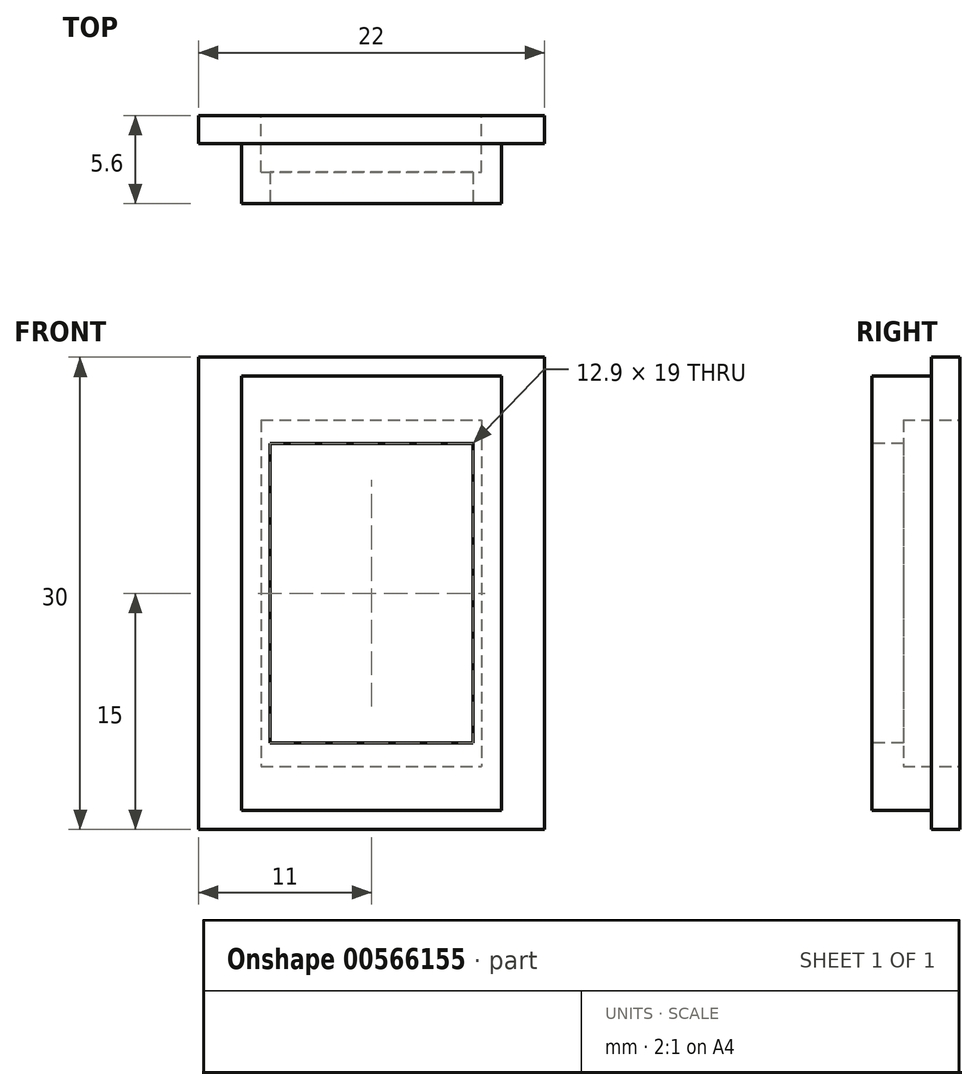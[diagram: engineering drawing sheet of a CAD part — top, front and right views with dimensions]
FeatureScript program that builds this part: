
annotation { "Feature Type Name" : "Feature", "Feature Type Description" : "" }
export const myFeature = defineFeature(function(context is Context, id is Id, definition is map)
    precondition{}
    {
        {
            var Q0;
            Q0=qCreatedBy(makeId("Front.planeOp"),FACE);
            var sketch = newSketch(context, id + "F0", { "sketchPlane" : qUnion([Q0])});
            skLineSegment(sketch, "E0.bottom", {"start": v(11, 15) * mm, "end": v(-11, 15) * mm});
            skLineSegment(sketch, "E0.top", {"start": v(11, -15) * mm, "end": v(-11, -15) * mm});
            skLineSegment(sketch, "E0.left", {"start": v(11, 15) * mm, "end": v(11, -15) * mm});
            skLineSegment(sketch, "E0.right", {"start": v(-11, 15) * mm, "end": v(-11, -15) * mm});
            skPoint(sketch, "E0.middle", {"position": v(0, 0) * mm});
            skSolve(sketch);
        }
        {
            var Q0;
            Q0 = qSketchRegion(id + "F0", true);
            extrude(context, id + "F1", {"entities" : qUnion([Q0]), "depth" : 1.8 * mm, "offsetDistance" : 25 * mm});
        }
        {
            var Q0;
            Q0=makeQuery(id+"F1.opExtrude","CAP_FACE",FACE,{"disambiguationData":[OSD([sQuery(id+"F0.wireOp",EDGE,"E0.bottom"),sQuery(id+"F0.wireOp",EDGE,"E0.top"),sQuery(id+"F0.wireOp",EDGE,"E0.left"),sQuery(id+"F0.wireOp",EDGE,"E0.right")])],"isStart":false});
            var sketch = newSketch(context, id + "F2", { "sketchPlane" : qUnion([Q0])});
            skLineSegment(sketch, "E1.bottom", {"start": v(8.25, 13.8) * mm, "end": v(-8.25, 13.8) * mm});
            skLineSegment(sketch, "E1.top", {"start": v(8.25, -13.8) * mm, "end": v(-8.25, -13.8) * mm});
            skLineSegment(sketch, "E1.left", {"start": v(8.25, 13.8) * mm, "end": v(8.25, -13.8) * mm});
            skLineSegment(sketch, "E1.right", {"start": v(-8.25, 13.8) * mm, "end": v(-8.25, -13.8) * mm});
            skPoint(sketch, "E1.middle", {"position": v(0, 0) * mm});
            skSolve(sketch);
        }
        {
            var Q0;
            Q0 = qSketchRegion(id + "F2", true);
            extrude(context, id + "F3", {"entities" : qUnion([Q0]), "operationType" : NewBodyOperationType.ADD, "depth" : 3.8 * mm, "offsetDistance" : 25 * mm});
        }
        {
            var Q0;
            Q0=makeQuery(id+"F3.opExtrude","CAP_FACE",FACE,{"disambiguationData":[OSD([sQuery(id+"F2.wireOp",EDGE,"E1.bottom"),sQuery(id+"F2.wireOp",EDGE,"E1.top"),sQuery(id+"F2.wireOp",EDGE,"E1.left"),sQuery(id+"F2.wireOp",EDGE,"E1.right")])],"isStart":false});
            var sketch = newSketch(context, id + "F4", { "sketchPlane" : qUnion([Q0])});
            skLineSegment(sketch, "E2.bottom", {"start": v(6.45, 9.5) * mm, "end": v(-6.45, 9.5) * mm});
            skLineSegment(sketch, "E2.top", {"start": v(6.45, -9.5) * mm, "end": v(-6.45, -9.5) * mm});
            skLineSegment(sketch, "E2.left", {"start": v(6.45, 9.5) * mm, "end": v(6.45, -9.5) * mm});
            skLineSegment(sketch, "E2.right", {"start": v(-6.45, 9.5) * mm, "end": v(-6.45, -9.5) * mm});
            skPoint(sketch, "E2.middle", {"position": v(0, 0) * mm});
            skSolve(sketch);
        }
        {
            var Q0;
            Q0 = qSketchRegion(id + "F4", true);
            extrude(context, id + "F5", {"entities" : qUnion([Q0]), "operationType" : NewBodyOperationType.REMOVE, "oppositeDirection" : true, "depth" : 25 * mm, "offsetDistance" : 25 * mm});
        }
        {
            var Q0;
            Q0=makeQuery(id+"F1.opExtrude","CAP_FACE",FACE,{"disambiguationData":[OSD([sQuery(id+"F0.wireOp",EDGE,"E0.bottom"),sQuery(id+"F0.wireOp",EDGE,"E0.top"),sQuery(id+"F0.wireOp",EDGE,"E0.left"),sQuery(id+"F0.wireOp",EDGE,"E0.right")])],"isStart":true});
            var sketch = newSketch(context, id + "F6", { "sketchPlane" : qUnion([Q0])});
            skLineSegment(sketch, "E3.0", {"start": v(-8.25, 13.8) * mm, "end": v(8.25, 13.8) * mm, "construction": true});
            skLineSegment(sketch, "E3.1", {"start": v(-8.25, 13.8) * mm, "end": v(-8.25, -13.8) * mm, "construction": true});
            skLineSegment(sketch, "E3.2", {"start": v(8.25, 13.8) * mm, "end": v(8.25, -13.8) * mm, "construction": true});
            skLineSegment(sketch, "E3.3", {"start": v(-8.25, -13.8) * mm, "end": v(8.25, -13.8) * mm, "construction": true});
            skLineSegment(sketch, "E4.bottom", {"start": v(7, 11) * mm, "end": v(-7, 11) * mm});
            skLineSegment(sketch, "E4.top", {"start": v(7, -11) * mm, "end": v(-7, -11) * mm});
            skLineSegment(sketch, "E4.left", {"start": v(7, 11) * mm, "end": v(7, -11) * mm});
            skLineSegment(sketch, "E4.right", {"start": v(-7, 11) * mm, "end": v(-7, -11) * mm});
            skPoint(sketch, "E4.middle", {"position": v(0, 0) * mm});
            skSolve(sketch);
        }
        {
            var Q0;
            Q0 = qSketchRegion(id + "F6", true);
            extrude(context, id + "F7", {"entities" : qUnion([Q0]), "operationType" : NewBodyOperationType.REMOVE, "oppositeDirection" : true, "depth" : 3.6 * mm, "offsetDistance" : 25 * mm});
        }
    });
